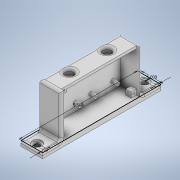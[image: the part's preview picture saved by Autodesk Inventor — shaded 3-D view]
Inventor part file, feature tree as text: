
AUTODESK INVENTOR PART (.ipt)
format: ipt  version: 2020 (Build 240168000, 168)  size: 395,264 bytes
history: native  units: in
note: dims shown in document units (in); Inventor stores cm internally (conversion verified against a paired STEP export)
features: sketch x11, extrude x7, hole x5, fillet x2, projected_geometry x2
ambient origin geometry x8: Origin, YZ Plane, XZ Plane, XY Plane, X Axis, Y Axis, Z Axis, Center Point
bodies: Solid1 (feature_tree)
feature tree (27):
  sketch  "Sketch1"  dims[d0=1.0in d1=5.5in]
  extrude  "Extrusion1"  Depth=5.5in
  hole  "Hole1"  [1 undecoded]
  extrude  "Extrusion2"  Depth=1.0in
  extrude  "Extrusion3"  Depth=0.125in
  extrude  "Extrusion4"  Depth=0.125in
  hole  "Hole2"  [1 undecoded]
  hole  "Hole3"  [1 undecoded]
  extrude  "Extrusion6"  Depth=0.125in TaperAngle=0.0deg
  extrude  "Extrusion7"  Depth=0.875in
  extrude  "Extrusion8"  Depth=0.125in
  hole  "Hole4"  [1 undecoded]
  hole  "Hole5"  [1 undecoded]
  fillet  "Fillet1"  Radius=1.125in
  fillet  "Fillet2"  Radius=0.175in
  sketch  "Sketch2"  dims[d2=0.25in d3=0.25in]
  sketch  "Sketch3"  dims[d4=0.25in d5=0.0in]
  sketch  "Sketch4"  dims[d6=0.281in d7=0.75in d8=0.438in d9=0.0625in d10=0.5635in d11=0.25in d12=0.0in d13=1.0in]
  sketch  "Sketch5"  dims[d14=0.125in d15=3.5in]
  projected_geometry  "Projected Loop1"
  sketch  "Sketch6"  dims[d16=1.0in d17=0.125in]
  projected_geometry  "Projected Loop2"
  sketch  "Sketch8"  dims[d18=1.0in d19=0.125in]
  sketch  "Sketch9"  dims[d20=2.0in d21=0.0in d22=3.5in]
  sketch  "Sketch10"  dims[d23=0.125in d24=0.75in d25=0.0in]
  sketch  "Sketch11"  dims[d26=0.9375in d27=0.875in]
  sketch  "Sketch12"  dims[d28=1.75in d29=1.025in d30=1.125in d31=1.025in d32=1.125in d33=0.175in d34=0.175in d35=0.175in d36=0.175in d37=0.175in d38=0.175in d39=0.175in d40=0.25in d41=0.0in d42=0.07in d43=0.75in d44=0.438in d45=0.25in d46=0.5635in d47=0.375in d48=0.0in d49=1.225in d50=1.325in d51=1.225in d52=1.325in d53=0.425in d54=0.425in d55=0.4in d56=0.75in d57=0.438in d58=0.25in d59=0.5635in d60=0.375in d61=0.0in d66=0.125in d67=0.125in d68=0.125in d69=0.125in d70=0.325in d71=0.25in d72=0.0in d73=0.25in d74=0.25in d75=0.25in d76=0.25in d77=0.25in d78=0.25in d79=0.0in d80=0.25in d81=0.125in d82=0.25in d83=0.25in d84=0.25in d85=0.0in d86=0.125in d87=0.125in d88=0.125in d89=0.089in d90=0.75in d91=0.438in d92=0.25in d93=0.5635in d94=0.375in d95=0.0in d96=0.125in d97=0.125in d98=0.125in d99=0.125in d100=0.125in d101=0.125in d102=0.125in d103=0.089in d104=0.75in d105=0.438in d106=0.25in d107=0.5635in d108=0.25in d109=0.0in d110=0.125in d111=0.125in d62=0.5in d63=0.0344in d64=0.5in d65=0.0344in]
note: 5 required parameter values undecoded (feature->parameter linkage not recoverable at this tier; creation-order binding heuristic only, values carry confidence <= 0.55)
